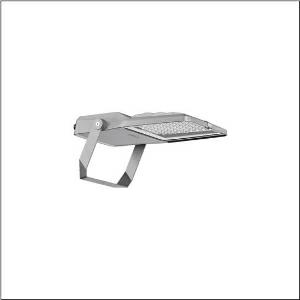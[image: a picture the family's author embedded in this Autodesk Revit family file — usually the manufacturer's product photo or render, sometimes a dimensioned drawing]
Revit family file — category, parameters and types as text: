
# Revit family: floodlight_fl_21_mini___pl61_5xa7771c2c1a_7983
name_source: partatom
category: Lighting Fixtures
units: mm (PartAtom-declared; Revit-internal decimal feet)

## family parameters
Cut with Voids When Loaded = No
Host = Face
Light Source = No
Part Type = Normal
Room Calculation Point = No
Round Connector Dimension = Use Diameter
Shared = No

## types (1)
- --- (1 x LED, 11980 lm, 87.2 W, 3000K)
    Apparent Load = 87 VA
    CIE Flux Codes = 33 65 98 100 100
    Color Rendering = 70
    Color Temperature = 3000K
    Default Elevation = 1800 mm
    Description = Floodlight FL 21 mini, floodlight, primary light control with lens, of PMMA, primary optical cover: protective disc, of toughened safety glass, transparent, light distribution: PL61, light emission: direct distribution, installation type: surface-mounted, LED, High Power LED, rated luminous flux: 11.980lm, luminous efficacy: 137lm/W, light colour: 730, colour temperature: 3000K, control gear: ECG iQ, control: Auto-Match, Temp-Guard, Lumen-Switch, Night-Set, Smart-Wire, Light-Fading, Desk-Remote (wireless, voltage-free reading and setting of iQ features in the workshop via application-optimized NFC function/RFID function), optimised constant luminous flux control (CLO 2.0), with terminal, 6-pole, mains connection: 220..240V, AC, 50/60Hz, start of lifetime: 87W, end of lifetime: 92W, reduction: 40W, luminaire housing, of diecast aluminium, powder-coated, Siteco® metallic grey (DB 702S), corrosivity category C5 according to DIN EN ISO 12944, mounting bracket, of steel, galvanised, powder-coated, Siteco® metallic grey (DB 702S), protection rating (complete): IP66, insulation class (complete): insulation class II (safety insulation), certification: CE, ENEC, VDE, protection symbol: D, impact resistance: IK08, permissible operating ambient temperature: -40..+40°C, permissible operating ambient temperature for outdoor applications: -40..+50°C, standard: DIN EN 12944, packaging unit: 1 piece

Light Distribution: PL61
    Height = 70 mm
    Lamp = 1 x LED
    Lamp Light Flux = 11980 lm
    Lamp Power = 87.2 W
    Lamp count = 1
    Length = 485 mm
    Luminous efficacy = 137 lm/W
    Manufacturer = Siteco
    ModVariant = No
    Model = 5XA7771C2C1A
    Number of Poles = 1
    OnlyDefault = Yes
    Power Factor = 1
    Product Name = Floodlight FL 21 mini | PL61
    Product group = floodlight | pylon top
    ProductGroupID = 6101
    Protection Class = Protection class II
    Protection Degree = IP 66
    RLX_Detail_Level = 1
    RlxData = <blob elided: 96281 chars, md5=1711649b>
    Socket = socket
    Standby Power = 0 W
    System Light Flux = 11980 lm
    System Power = 87 W
    Type Comments = factory setting: luminous flux: 100 % | dim-lin: 254 | 456 mA
    Type Image = l_1006845.jpg
    URL = http://relux.com
    VarID = @adj_085693
    Voltage = 0 V
    Weight = 0.00 kg
    Width = 337 mm

## geometry (parser evidence)
native form markers: Blend x4, Sweep x13
no freeform markers — native parametric forms only
